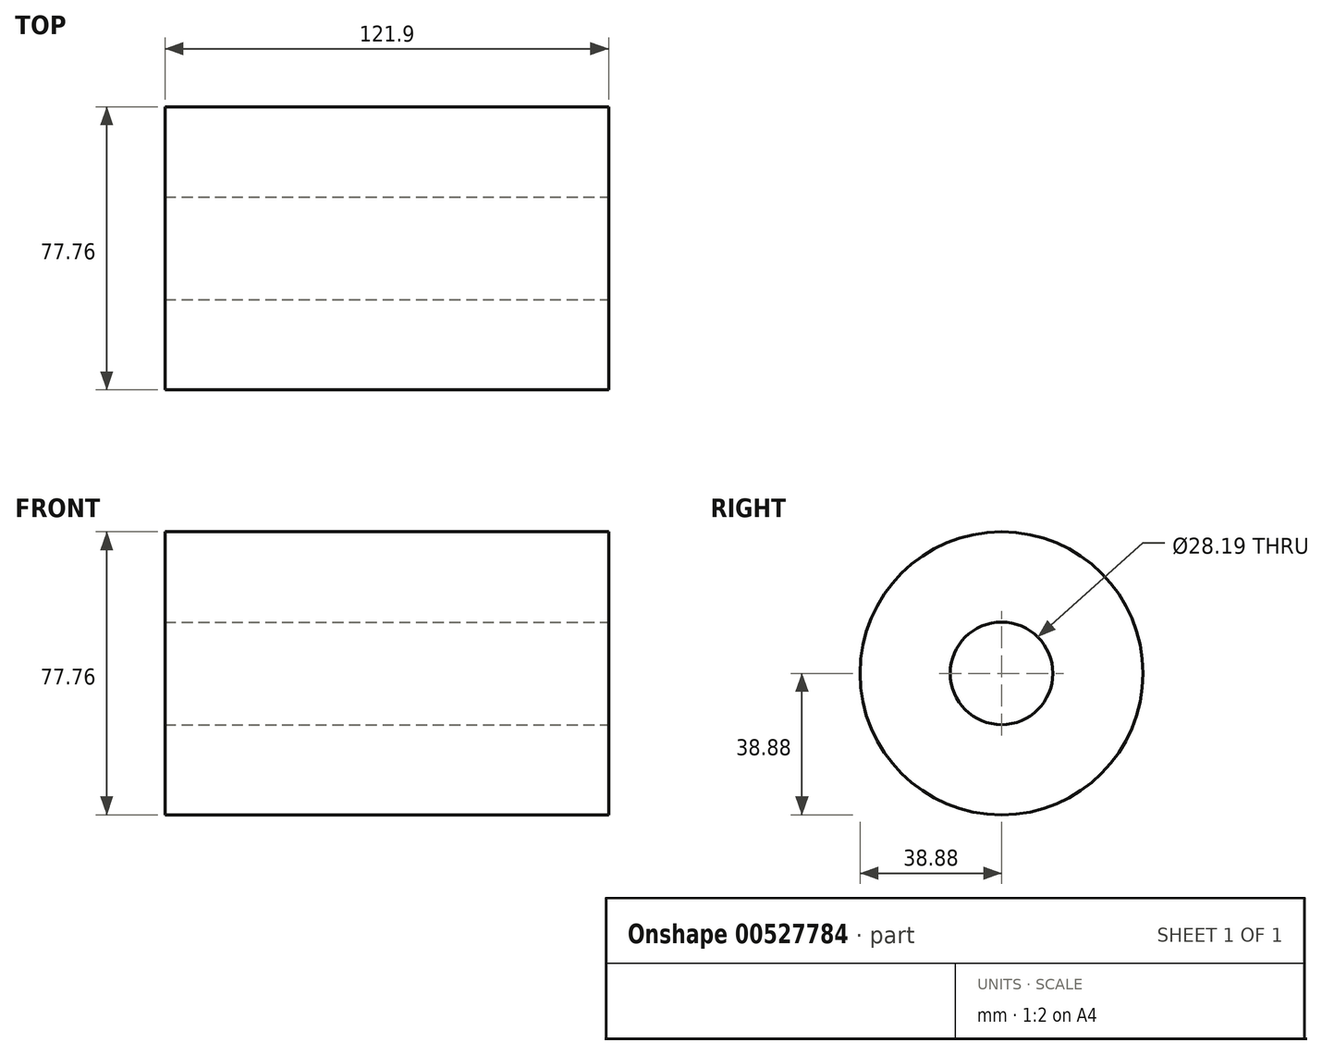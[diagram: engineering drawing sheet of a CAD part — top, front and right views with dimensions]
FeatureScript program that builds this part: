
annotation { "Feature Type Name" : "Feature", "Feature Type Description" : "" }
export const myFeature = defineFeature(function(context is Context, id is Id, definition is map)
    precondition{}
    {
        {
            var Q0;
            Q0=qCreatedBy(makeId("Front.planeOp"),FACE);
            var sketch = newSketch(context, id + "F0", { "sketchPlane" : qUnion([Q0])});
            skLineSegment(sketch, "E0.bottom", {"start": v(45.35, 38.88) * mm, "end": v(-76.55, 38.88) * mm});
            skLineSegment(sketch, "E0.top", {"start": v(45.35, 14.1) * mm, "end": v(-76.55, 14.1) * mm});
            skLineSegment(sketch, "E0.left", {"start": v(45.35, 38.88) * mm, "end": v(45.35, 14.1) * mm});
            skLineSegment(sketch, "E0.right", {"start": v(-76.55, 38.88) * mm, "end": v(-76.55, 14.1) * mm});
            skLineSegment(sketch, "E1", {"start": v(0, 0) * mm, "end": v(-113.72, 0) * mm});
            skSolve(sketch);
        }
        {
            var Q0;
            Q0 = qSketchRegion(id + "F0", true);
            var Q1;
            Q1=sQuery(id+"F0.wireOp",EDGE,"E1");
            revolve(context, id + "F1", {"entities" : qUnion([Q0]), "axis" : qUnion([Q1]), "revolveType" : RevolveType.FULL});
        }
    });
